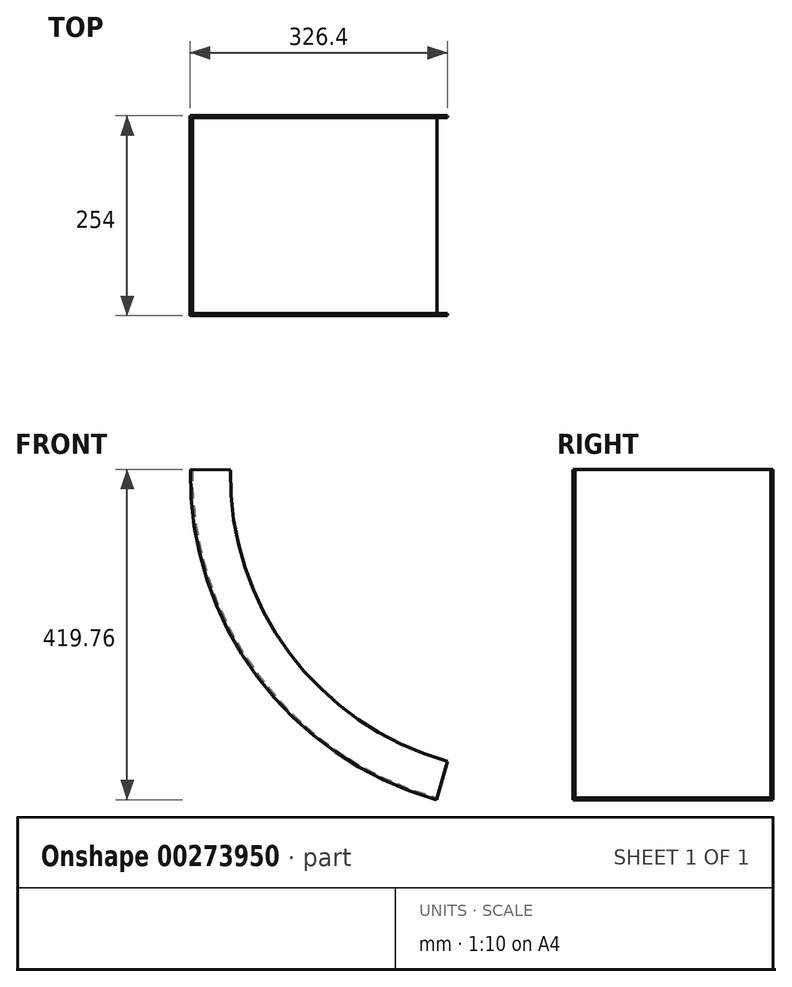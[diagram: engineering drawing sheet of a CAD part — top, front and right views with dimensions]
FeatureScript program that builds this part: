
annotation { "Feature Type Name" : "Feature", "Feature Type Description" : "" }
export const myFeature = defineFeature(function(context is Context, id is Id, definition is map)
    precondition{}
    {
        {
            var Q0;
            Q0=qCreatedBy(makeId("Front.planeOp"),FACE);
            var sketch = newSketch(context, id + "F0", { "sketchPlane" : qUnion([Q0])});
            skCircle(sketch, "E0", {"center": v(0, 0) * mm, "radius": 406.4 * mm, "construction": true});
            skLineSegment(sketch, "E1", {"start": v(0, 0) * mm, "end": v(0, -543.6) * mm, "construction": true});
            skLineSegment(sketch, "E2", {"start": v(0, 0) * mm, "end": v(-154.2, -528.8) * mm, "construction": true});
            skArc(sketch, "E3", {"start": v(-435.02, 0) * mm, "mid": v(-350.3, -263.2) * mm, "end": v(-122.4, -419.76) * mm});
            skArc(sketch, "E4.0", {"start": v(-384.23, -0.88) * mm, "mid": v(-309.55, -232.85) * mm, "end": v(-108.69, -370.84) * mm});
            skLineSegment(sketch, "E5", {"start": v(-435.02, 0) * mm, "end": v(-384.23, -0.88) * mm});
            skLineSegment(sketch, "E6", {"start": v(-108.69, -370.84) * mm, "end": v(-122.4, -419.76) * mm});
            skLineSegment(sketch, "E7", {"start": v(-108.69, -370.84) * mm, "end": v(-122.4, -419.76) * mm, "construction": true});
            skLineSegment(sketch, "E8.0", {"start": v(-133.15, -364) * mm, "end": v(-146.85, -412.9) * mm, "construction": true});
            skSolve(sketch);
        }
        {
            var Q0;
            Q0 = qSketchRegion(id + "F0", true);
            extrude(context, id + "F1", {"entities" : qUnion([Q0]), "depth" : 254 * mm});
        }
        {
            var Q0;
            Q0=makeQuery(id+"F1.opExtrude","SWEPT_FACE",FACE,{"disambiguationData":[OSD([sQuery(id+"F0.wireOp",EDGE,"E4.0")])]});
            var Q1;
            Q1=makeQuery(id+"F1.opExtrude","SWEPT_FACE",FACE,{"disambiguationData":[OSD([sQuery(id+"F0.wireOp",EDGE,"E6")])]});
            var Q2;
            Q2=makeQuery(id+"F1.opExtrude","SWEPT_FACE",FACE,{"disambiguationData":[OSD([sQuery(id+"F0.wireOp",EDGE,"E5")])]});
            shell(context, id + "F2", {"entities" : qUnion([Q0, Q1, Q2]), "thickness" : 2.54 * mm});
        }
    });
